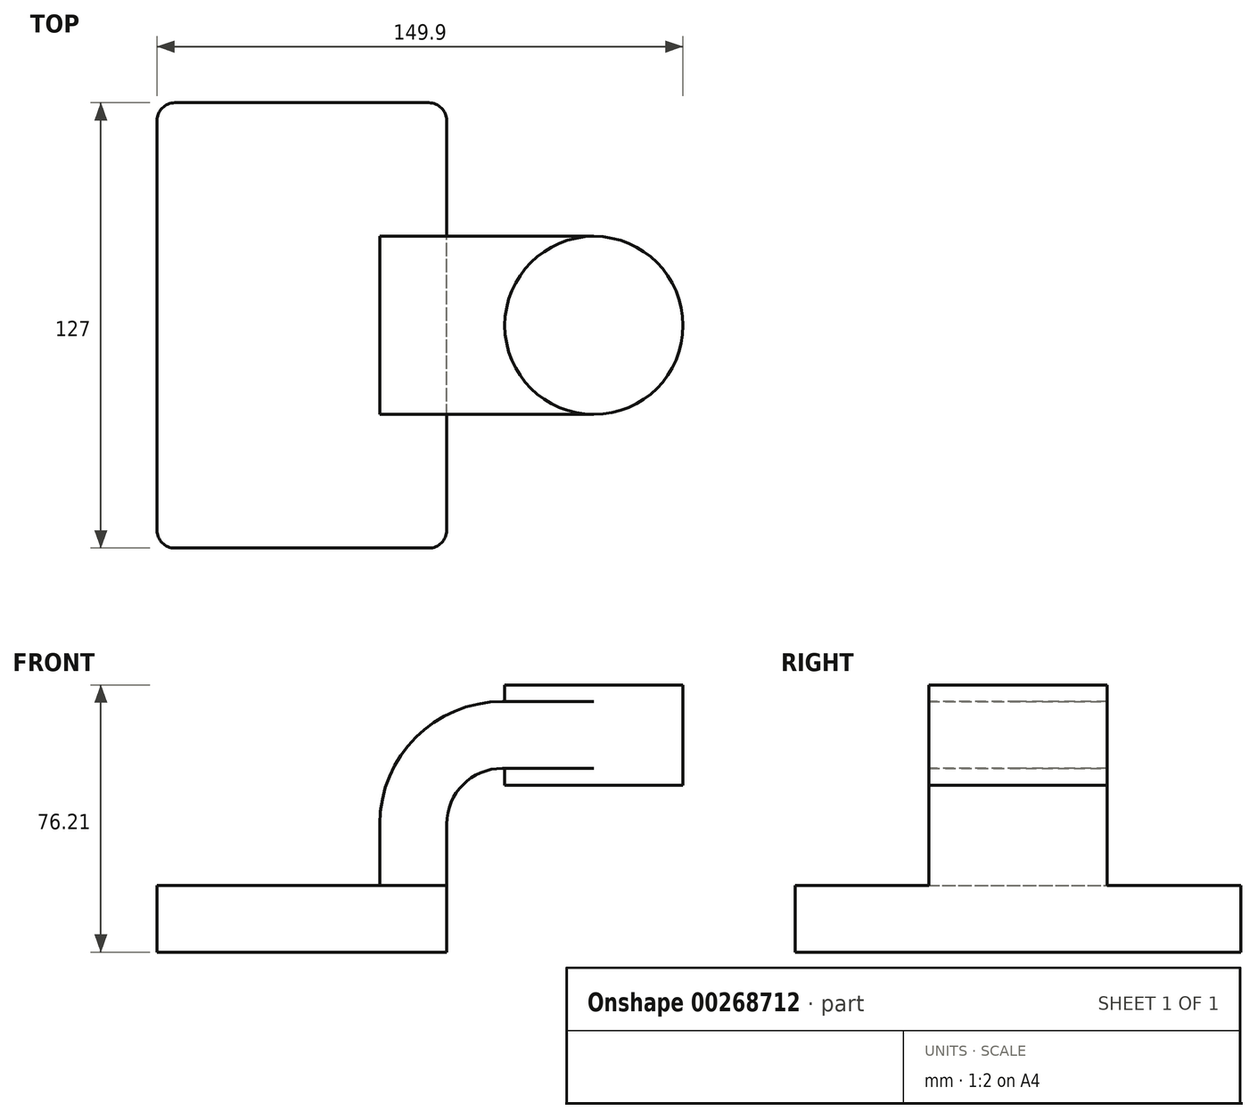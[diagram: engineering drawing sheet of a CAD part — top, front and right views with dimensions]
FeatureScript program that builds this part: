
annotation { "Feature Type Name" : "Feature", "Feature Type Description" : "" }
export const myFeature = defineFeature(function(context is Context, id is Id, definition is map)
    precondition{}
    {
        {
            var Q0;
            Q0=qCreatedBy(makeId("Front.planeOp"),FACE);
            var sketch = newSketch(context, id + "F0", { "sketchPlane" : qUnion([Q0])});
            skPoint(sketch, "E0.middle", {"position": v(0, 0) * mm});
            skLineSegment(sketch, "E1.bottom", {"start": v(41.27, 9.53) * mm, "end": v(-41.28, 9.53) * mm});
            skLineSegment(sketch, "E1.top", {"start": v(41.28, -9.52) * mm, "end": v(-41.27, -9.52) * mm});
            skLineSegment(sketch, "E1.left", {"start": v(41.28, 9.53) * mm, "end": v(41.28, -9.52) * mm});
            skLineSegment(sketch, "E1.right", {"start": v(-41.28, 9.53) * mm, "end": v(-41.28, -9.52) * mm});
            skLineSegment(sketch, "E2", {"start": v(41.27, 9.53) * mm, "end": v(41.27, 27) * mm});
            skArc(sketch, "E3", {"start": v(41.27, 27) * mm, "mid": v(45.92, 38.23) * mm, "end": v(57.15, 42.88) * mm});
            skLineSegment(sketch, "E4.bottom", {"start": v(108.63, 66.68) * mm, "end": v(57.83, 66.68) * mm});
            skLineSegment(sketch, "E4.top", {"start": v(108.63, 38.1) * mm, "end": v(57.83, 38.1) * mm});
            skLineSegment(sketch, "E4.left", {"start": v(108.63, 66.68) * mm, "end": v(108.63, 38.1) * mm});
            skLineSegment(sketch, "E4.right", {"start": v(57.83, 66.68) * mm, "end": v(57.83, 38.1) * mm});
            skPoint(sketch, "E4.middle", {"position": v(83.23, 52.39) * mm});
            skLineSegment(sketch, "E5", {"start": v(57.15, 42.88) * mm, "end": v(83.23, 42.88) * mm});
            skLineSegment(sketch, "E6.0", {"start": v(57.15, 61.93) * mm, "end": v(83.23, 61.93) * mm});
            skArc(sketch, "E6.1", {"start": v(22.22, 27) * mm, "mid": v(32.45, 51.7) * mm, "end": v(57.15, 61.93) * mm});
            skLineSegment(sketch, "E6.2", {"start": v(22.22, 9.53) * mm, "end": v(22.22, 27) * mm});
            skLineSegment(sketch, "E7", {"start": v(83.23, 38.1) * mm, "end": v(83.23, 66.68) * mm});
            skFitSpline(sketch, "E8", {"points": [v(-41.28, 9.53) * mm, v(57.15, 61.93) * mm], "startDerivative": vector(4.72, 100.2) * mm, "endDerivative": vector(110.73, -16.9) * mm});
            skSolve(sketch);
        }
        {
            var Q0;
            Q0=makeQuery(id+"F0.imprint","IMPRINT",FACE,{"disambiguationData":[TD([[makeQuery(id+"F0.imprint","IMPRINT",EDGE,{"derivedFrom":sQuery(id+"F0.wireOp",EDGE,"E1.top")}),-1.0]])]});
            extrude(context, id + "F1", {"entities" : qUnion([Q0]), "endBound" : BoundingType.SYMMETRIC, "depth" : 127 * mm});
        }
        {
            var Q0;
            {var subQ7=sQuery(id+"F0.wireOp",EDGE,"E2");Q0=makeQuery(id+"F0.imprint","IMPRINT",FACE,{"disambiguationData":[TD([[makeQuery(id+"F0.imprint","IMPRINT",EDGE,{"derivedFrom":subQ7}),1.0]])]});}
            var Q1;
            {var subQ0=sQuery(id+"F0.wireOp",EDGE,"E6.0");var subQ1=sQuery(id+"F0.wireOp",EDGE,"E4.right");var subQ2=makeQuery(id+"F0.imprint","INTERSECT",VERTEX,{"derivedFrom":[subQ1,subQ0]});Q1=makeQuery(id+"F0.imprint","IMPRINT",FACE,{"disambiguationData":[TD([[makeQuery(id+"F0.imprint","IMPRINT",EDGE,{"disambiguationData":[TD([[subQ2,-1.0]])],"derivedFrom":subQ1}),1.0]])]});}
            extrude(context, id + "F2", {"entities" : qUnion([Q0, Q1]), "operationType" : NewBodyOperationType.ADD, "endBound" : BoundingType.SYMMETRIC, "depth" : 50.8 * mm});
        }
        {
            var Q0;
            Q0=makeQuery(id+"F0.imprint","IMPRINT",FACE,{"disambiguationData":[TD([[makeQuery(id+"F0.imprint","IMPRINT",EDGE,{"derivedFrom":sQuery(id+"F0.wireOp",EDGE,"E6.1")}),1.0]])]});
            extrude(context, id + "F3", {"entities" : qUnion([Q0]), "operationType" : NewBodyOperationType.ADD, "endBound" : BoundingType.SYMMETRIC, "depth" : 15.88 * mm});
        }
        {
            var Q0;
            {var subQ0=sQuery(id+"F0.wireOp",EDGE,"E4.left");Q0=makeQuery(id+"F0.imprint","IMPRINT",FACE,{"disambiguationData":[TD([[makeQuery(id+"F0.imprint","IMPRINT",EDGE,{"derivedFrom":subQ0}),-1.0]])]});}
            var Q1;
            Q1=sQuery(id+"F0.wireOp",EDGE,"E7");
            revolve(context, id + "F4", {"operationType" : NewBodyOperationType.ADD, "entities" : qUnion([Q0]), "axis" : qUnion([Q1]), "revolveType" : RevolveType.FULL});
        }
        {
            var Q0;
            Q0=makeQuery(id+"F1.opExtrude","CAP_EDGE",EDGE,{"disambiguationData":[OSD([sQuery(id+"F0.wireOp",EDGE,"E1.right")])],"isStart":false});
            var Q1;
            Q1=makeQuery(id+"F1.opExtrude","CAP_EDGE",EDGE,{"disambiguationData":[OSD([sQuery(id+"F0.wireOp",EDGE,"E1.left")])],"isStart":false});
            var Q2;
            Q2=makeQuery(id+"F1.opExtrude","CAP_EDGE",EDGE,{"disambiguationData":[OSD([sQuery(id+"F0.wireOp",EDGE,"E1.right")])],"isStart":true});
            var Q3;
            Q3=makeQuery(id+"F1.opExtrude","CAP_EDGE",EDGE,{"disambiguationData":[OSD([sQuery(id+"F0.wireOp",EDGE,"E1.left")])],"isStart":true});
            fillet(context, id + "F5", {"entities" : qUnion([Q0, Q1, Q2, Q3]), "radius" : 5.08 * mm, "tangentPropagation" : true, "allowEdgeOverflow" : false});
        }
    });
